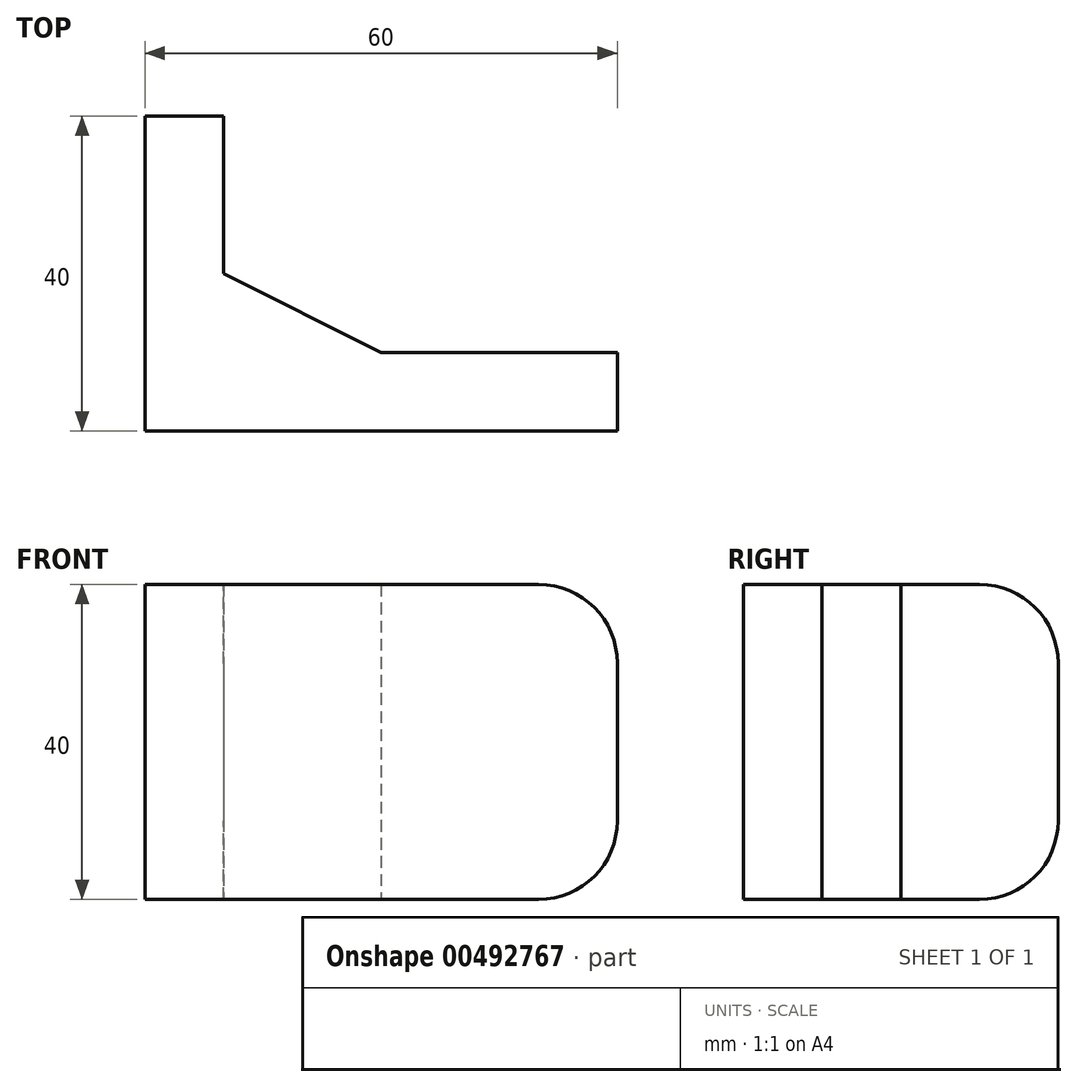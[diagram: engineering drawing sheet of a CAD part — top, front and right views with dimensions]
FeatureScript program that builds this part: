
annotation { "Feature Type Name" : "Feature", "Feature Type Description" : "" }
export const myFeature = defineFeature(function(context is Context, id is Id, definition is map)
    precondition{}
    {
        {
            var Q0;
            Q0=qCreatedBy(makeId("Top.planeOp"),FACE);
            var sketch = newSketch(context, id + "F0", { "sketchPlane" : qUnion([Q0])});
            skLineSegment(sketch, "E0", {"start": v(0, 0) * mm, "end": v(0, 40) * mm});
            skLineSegment(sketch, "E1", {"start": v(0, 40) * mm, "end": v(10, 40) * mm});
            skLineSegment(sketch, "E2", {"start": v(10, 40) * mm, "end": v(10, 20) * mm});
            skLineSegment(sketch, "E3", {"start": v(0, 0) * mm, "end": v(60, 0) * mm});
            skLineSegment(sketch, "E4", {"start": v(60, 0) * mm, "end": v(60, 10) * mm});
            skLineSegment(sketch, "E5", {"start": v(60, 10) * mm, "end": v(30, 10) * mm});
            skLineSegment(sketch, "E6", {"start": v(30, 10) * mm, "end": v(10, 20) * mm});
            skSolve(sketch);
        }
        {
            var Q0;
            Q0=makeQuery(id+"F0.imprint","IMPRINT",FACE,{"disambiguationData":[TD([[makeQuery(id+"F0.imprint","IMPRINT",EDGE,{"derivedFrom":sQuery(id+"F0.wireOp",EDGE,"E0")}),-1.0]])]});
            extrude(context, id + "F1", {"entities" : qUnion([Q0]), "depth" : 40 * mm});
        }
        {
            var Q0;
            Q0=makeQuery(id+"F1.opExtrude","CAP_EDGE",EDGE,{"disambiguationData":[OSD([sQuery(id+"F0.wireOp",EDGE,"E1")])],"isStart":false});
            var Q1;
            Q1=makeQuery(id+"F1.opExtrude","CAP_EDGE",EDGE,{"disambiguationData":[OSD([sQuery(id+"F0.wireOp",EDGE,"E1")])],"isStart":true});
            var Q2;
            Q2=makeQuery(id+"F1.opExtrude","CAP_EDGE",EDGE,{"disambiguationData":[OSD([sQuery(id+"F0.wireOp",EDGE,"E4")])],"isStart":false});
            var Q3;
            Q3=makeQuery(id+"F1.opExtrude","CAP_EDGE",EDGE,{"disambiguationData":[OSD([sQuery(id+"F0.wireOp",EDGE,"E4")])],"isStart":true});
            fillet(context, id + "F2", {"entities" : qUnion([Q0, Q1, Q2, Q3]), "radius" : 10 * mm, "tangentPropagation" : true, "allowEdgeOverflow" : false});
        }
    });
